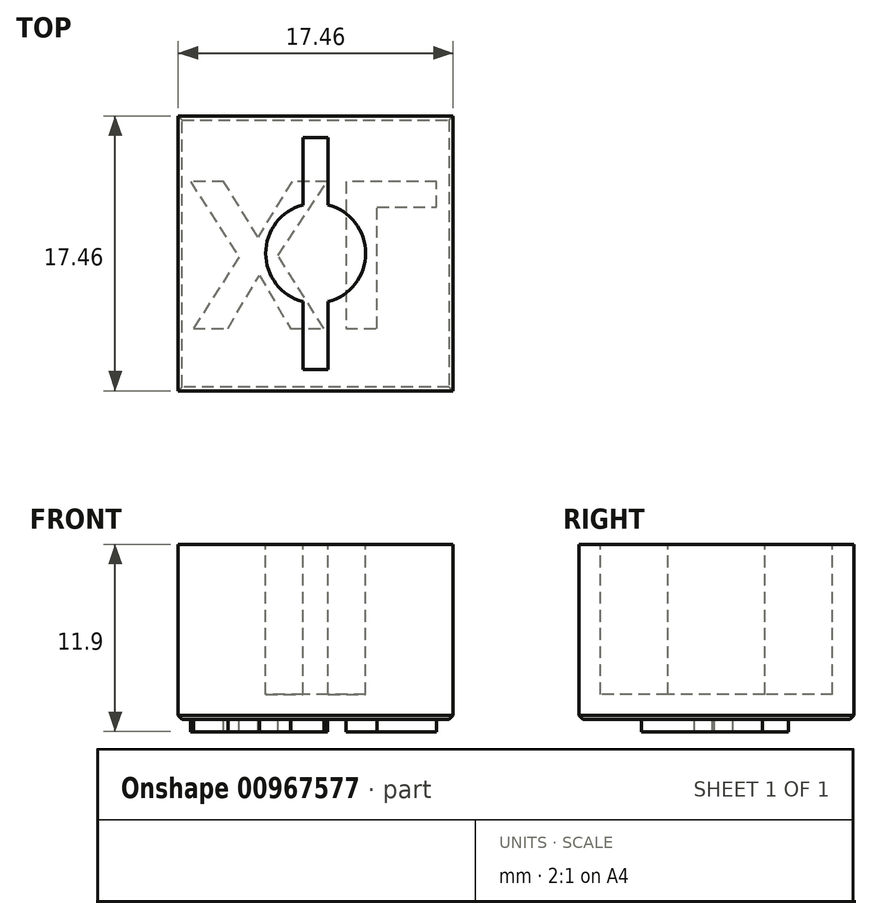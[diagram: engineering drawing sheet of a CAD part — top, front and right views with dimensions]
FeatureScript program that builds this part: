
annotation { "Feature Type Name" : "Feature", "Feature Type Description" : "" }
export const myFeature = defineFeature(function(context is Context, id is Id, definition is map)
    precondition{}
    {
        {
            var Q0;
            Q0=qCreatedBy(makeId("Top.planeOp"),FACE);
            var sketch = newSketch(context, id + "F0", { "sketchPlane" : qUnion([Q0])});
            skLineSegment(sketch, "E0.bottom", {"start": v(8.73, 8.73) * mm, "end": v(-8.73, 8.73) * mm});
            skLineSegment(sketch, "E0.top", {"start": v(8.73, -8.73) * mm, "end": v(-8.73, -8.73) * mm});
            skLineSegment(sketch, "E0.left", {"start": v(8.73, 8.73) * mm, "end": v(8.73, -8.73) * mm});
            skLineSegment(sketch, "E0.right", {"start": v(-8.73, 8.73) * mm, "end": v(-8.73, -8.73) * mm});
            skPoint(sketch, "E0.middle", {"position": v(0, 0) * mm});
            skSolve(sketch);
        }
        {
            var Q0;
            Q0 = qSketchRegion(id + "F0", true);
            extrude(context, id + "F1", {"entities" : qUnion([Q0]), "depth" : 11.1 * mm, "offsetDistance" : 25.4 * mm});
        }
        {
            var Q0;
            Q0=makeQuery(id+"F1.opExtrude","CAP_FACE",FACE,{"disambiguationData":[OSD([sQuery(id+"F0.wireOp",EDGE,"E0.bottom"),sQuery(id+"F0.wireOp",EDGE,"E0.top"),sQuery(id+"F0.wireOp",EDGE,"E0.left"),sQuery(id+"F0.wireOp",EDGE,"E0.right")])],"isStart":false});
            var sketch = newSketch(context, id + "F2", { "sketchPlane" : qUnion([Q0])});
            skLineSegment(sketch, "E1.bottom", {"start": v(0.8, 7.37) * mm, "end": v(-0.8, 7.37) * mm});
            skLineSegment(sketch, "E1.top", {"start": v(0.8, -7.37) * mm, "end": v(-0.8, -7.37) * mm});
            skPoint(sketch, "E1.middle", {"position": v(0, 0) * mm});
            skArc(sketch, "E2", {"start": v(1.42, -2.84) * mm, "mid": v(3.18, 0) * mm, "end": v(1.42, 2.84) * mm});
            skLineSegment(sketch, "E3", {"start": v(-0.8, 7.37) * mm, "end": v(0, 7.37) * mm});
            skArc(sketch, "E4.trimOffspring", {"start": v(-1.42, 2.84) * mm, "mid": v(-3.18, 0) * mm, "end": v(-1.42, -2.84) * mm});
            skArc(sketch, "E5", {"start": v(-0.8, 3.07) * mm, "mid": v(-3.18, 0) * mm, "end": v(-0.8, -3.07) * mm});
            skLineSegment(sketch, "E6", {"start": v(-0.8, 7.37) * mm, "end": v(-0.8, 3.07) * mm});
            skLineSegment(sketch, "E7.MirrorCS", {"start": v(0.8, 7.37) * mm, "end": v(0.8, 3.07) * mm});
            skArc(sketch, "E8.trimOffspring", {"start": v(0.8, -3.07) * mm, "mid": v(3.18, 0) * mm, "end": v(0.8, 3.07) * mm});
            skLineSegment(sketch, "E9.trimOffspring", {"start": v(-0.8, -3.07) * mm, "end": v(-0.8, -7.37) * mm});
            skLineSegment(sketch, "E10.trimOffspring", {"start": v(0.8, -3.07) * mm, "end": v(0.8, -7.37) * mm});
            skSolve(sketch);
        }
        {
            var Q0;
            Q0=makeQuery(id+"F1.opExtrude","CAP_EDGE",EDGE,{"disambiguationData":[OSD([sQuery(id+"F0.wireOp",EDGE,"E0.right")])],"isStart":true});
            var Q1;
            Q1=makeQuery(id+"F1.opExtrude","CAP_EDGE",EDGE,{"disambiguationData":[OSD([sQuery(id+"F0.wireOp",EDGE,"E0.top")])],"isStart":true});
            var Q2;
            Q2=makeQuery(id+"F1.opExtrude","CAP_EDGE",EDGE,{"disambiguationData":[OSD([sQuery(id+"F0.wireOp",EDGE,"E0.left")])],"isStart":true});
            var Q3;
            Q3=makeQuery(id+"F1.opExtrude","CAP_EDGE",EDGE,{"disambiguationData":[OSD([sQuery(id+"F0.wireOp",EDGE,"E0.bottom")])],"isStart":true});
            chamfer(context, id + "F3", {"entities" : qUnion([Q0, Q1, Q2, Q3]), "width" : 0.25 * mm, "tangentPropagation" : true});
        }
        {
            var Q0;
            Q0 = qSketchRegion(id + "F2", true);
            extrude(context, id + "F4", {"entities" : qUnion([Q0]), "operationType" : NewBodyOperationType.REMOVE, "oppositeDirection" : true, "depth" : 9.52 * mm, "offsetDistance" : 25.4 * mm});
        }
        {
            var Q0;
            Q0=makeQuery(id+"F1.opExtrude","CAP_FACE",FACE,{"disambiguationData":[OSD([sQuery(id+"F0.wireOp",EDGE,"E0.bottom"),sQuery(id+"F0.wireOp",EDGE,"E0.top"),sQuery(id+"F0.wireOp",EDGE,"E0.left"),sQuery(id+"F0.wireOp",EDGE,"E0.right")])],"isStart":true});
            var sketch = newSketch(context, id + "F5", { "sketchPlane" : qUnion([Q0])});
            skText(sketch, "E11", { "text": "XL", "fontName": "OpenSans-Bold.ttf"});
            const initialGuessF5  = {"E11": [-0.00796, -0.00456, 1, 0, 0.0094]};
            skSetInitialGuess(sketch, initialGuessF5);
            skSolve(sketch);
        }
        {
            var Q0;
            Q0=makeQuery(id+"F5.imprint","IMPRINT",FACE,{"disambiguationData":[TD([[makeQuery(id+"F5.imprint","IMPRINT",EDGE,{"derivedFrom":sQuery(id+"F5.wireOp",EDGE,"E11.sketch_text.stroke-12")}),-1.0]])]});
            extrude(context, id + "F6", {"entities" : qUnion([Q0]), "operationType" : NewBodyOperationType.ADD, "depth" : 0.8 * mm, "offsetDistance" : 25.4 * mm});
        }
        {
            var Q0;
            Q0 = qSketchRegion(id + "F5", true);
            extrude(context, id + "F7", {"entities" : qUnion([Q0]), "operationType" : NewBodyOperationType.ADD, "depth" : 0.8 * mm, "offsetDistance" : 25.4 * mm});
        }
    });
